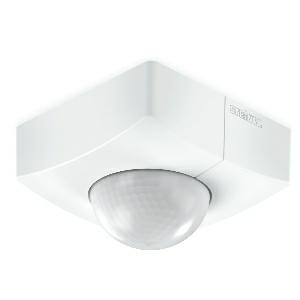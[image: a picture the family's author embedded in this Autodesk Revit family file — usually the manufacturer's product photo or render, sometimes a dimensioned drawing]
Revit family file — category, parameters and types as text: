
# Revit family: is_345_057275
name_source: partatom
category: Elektroinstallationen
revit_build: Autodesk Revit 2016 (Build: 20190508_0715(x64)
units: mm (PartAtom-declared; Revit-internal decimal feet)

## family parameters
Basisbauteil = Fläche
Beim Laden mit Abzugskörper schneiden = Nein
Bemaßung runder Anschluss = Durchmesser verwenden
Beschriftungsausrichtung beibehalten = Nein
Gemeinsam genutzt = Nein
Raumberechnungspunkt = Nein
Teiletyp = Normal

## types (1)
- IS 345
    Apparent Load = 0 VA
    Beschreibung = Type: Motion detectors; Dimensions (L x W x H): 65 x 95 x 95 mm; Mains power supply: 12 – 22,5 V / 50 – 60 Hz; Sensor Technology: passive infrared; Application, place: Outdoors, Indoors; Application, room: corridor / aisle, multi-storey / underground car park, outdoors, Indoors; Installation site: ceiling; Installation: Surface wiring; Switching zones: 280 switching zones; Electronic scalability: No; Mechanical scalability: No; Mounting height: 2,5 – 5 m; Optimum mounting height: 2,8 m; Detection angle: 360 °; Angle of aperture: 45 °; Sneak-by guard: Yes; Capability of masking out individual segments: Yes; Reach, radial: 12 x 6 m (72 m²); Reach, tangential: 23 x 6 m (138 m²); Twilight setting TEACH: Yes; Twilight setting: 2 – 1000 lx; Time setting: 5 sec – 15 min; Control output, Dali: Addressable/slave; Constant-lighting control: No; Basic light level function: No; Basic light level function time: 1-30 min, all night; With bus coupling: Yes; Settings via: Bus; With remote control: No; Interconnection: Yes; IP-rating: IP54; Material: Plastic; Ambient temperature: -20 – 50 °C; Colour: white; Colour, RAL: 9003; Manufacturer's Warranty: 5 years; Version: DALI-2 IPD - surface, sq.; PU1, EAN: 4007841057275
    Height = 95 mm
    Hersteller = Steinel
    Length = 65 mm
    Maximum range = 11.589 m
    ModVariant = Nein
    Modell = 057275
    Mounting Place = Ceiling
    Mounting Type = Surface mounted
    Number of Poles = 1
    OnlyDefault = Ja
    Power Factor = 1
    Product Name = IS 345
    Product group = Sensor-switched outdoor light
    ProductGroupID = 3
    Protection Class = Protection class
    Protection Degree = IP 54
    RlxData = <blob elided: 163949 chars, md5=ac331b3f>
    Sensor characteristics = Stretched
    Sensor type = Passive (infrared)
    SensorDataFile = <blob elided: 5885 chars, md5=98bccc25>
    Type of entry = Motion
    Typenbild = produkt1_057275.jpg
    Typenkommentare = Product without accessories
    URL = http://relux.com
    VarID = ---
    Voltage = 0 V
    Vorgabe-Ansicht = 1800 mm
    Weight = 0.00 kg
    Width = 95 mm

## geometry (parser evidence)
native form markers: Blend x4, Sweep x17
no freeform markers — native parametric forms only
